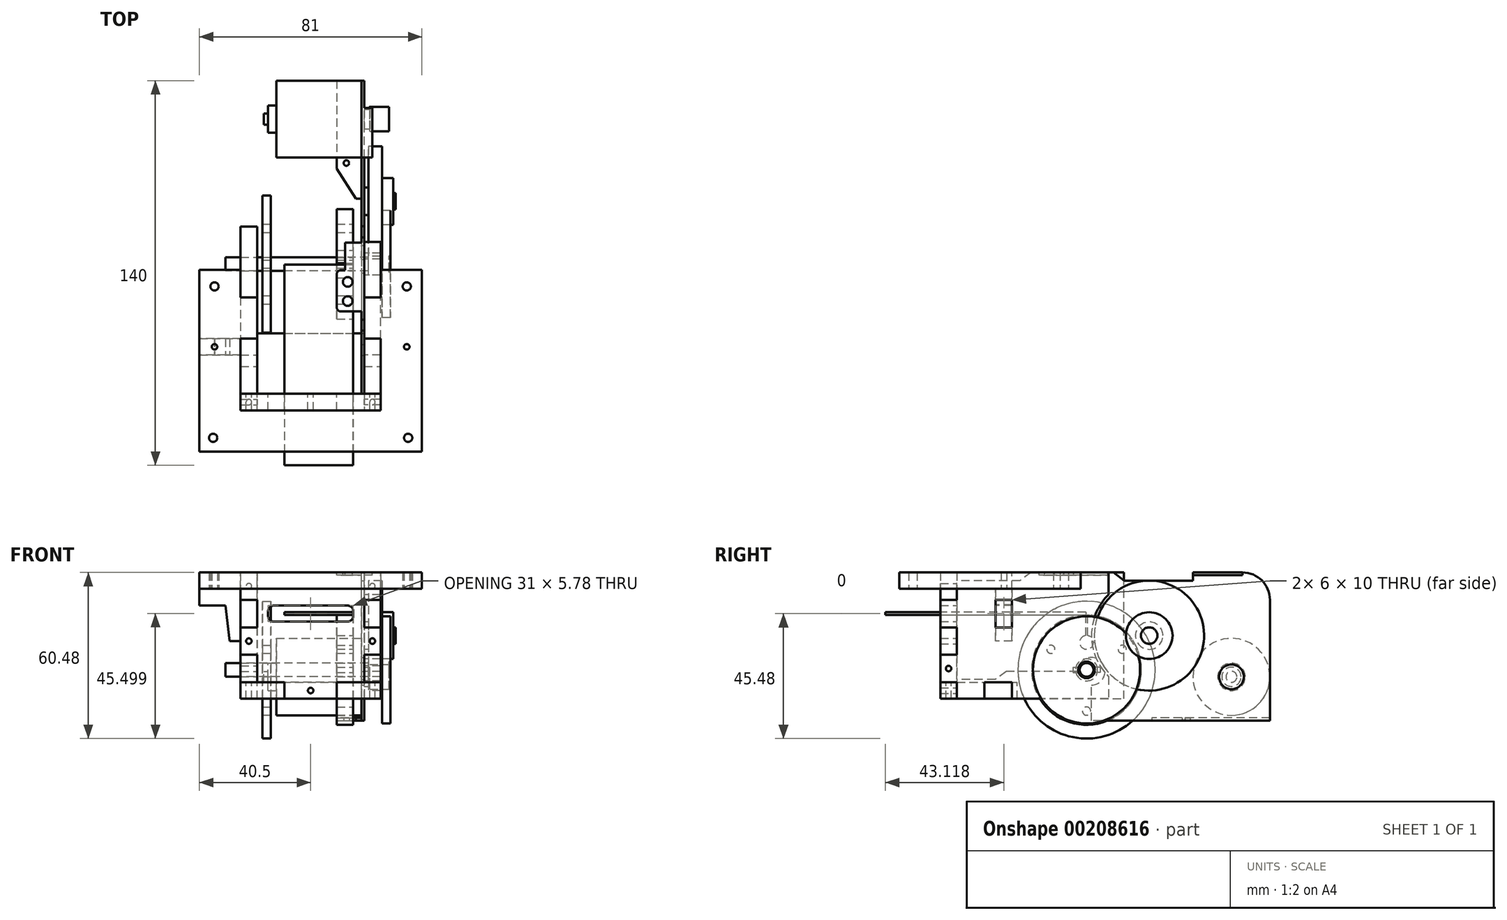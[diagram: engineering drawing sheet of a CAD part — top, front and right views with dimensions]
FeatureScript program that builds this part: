
annotation { "Feature Type Name" : "Feature", "Feature Type Description" : "" }
export const myFeature = defineFeature(function(context is Context, id is Id, definition is map)
    precondition{}
    {
        {
            var Q0;
            Q0=qCreatedBy(makeId("Top.planeOp"),FACE);
            var sketch = newSketch(context, id + "F0", { "sketchPlane" : qUnion([Q0])});
            skLineSegment(sketch, "E0.bottom", {"start": v(-32, 14) * mm, "end": v(0, 14) * mm});
            skLineSegment(sketch, "E0.left", {"start": v(-32, 14) * mm, "end": v(-32, 5) * mm});
            skLineSegment(sketch, "E0.right", {"start": v(0, 14) * mm, "end": v(0, 3.5) * mm});
            skLineSegment(sketch, "E1.top", {"start": v(0, 3.5) * mm, "end": v(2, 3.5) * mm});
            skLineSegment(sketch, "E2.top", {"start": v(2, 4.5) * mm, "end": v(9, 4.5) * mm});
            skLineSegment(sketch, "E2.left", {"start": v(2, 3.5) * mm, "end": v(2, 4.5) * mm});
            skLineSegment(sketch, "E2.right", {"start": v(9, 0) * mm, "end": v(9, 4.5) * mm});
            skLineSegment(sketch, "E3", {"start": v(-36.5, 0) * mm, "end": v(-36.5, 2) * mm});
            skLineSegment(sketch, "E4", {"start": v(-36.5, 2) * mm, "end": v(-35, 2) * mm});
            skLineSegment(sketch, "E5", {"start": v(-35, 2) * mm, "end": v(-35, 5) * mm});
            skLineSegment(sketch, "E6", {"start": v(-35, 5) * mm, "end": v(-32, 5) * mm});
            skLineSegment(sketch, "E7", {"start": v(9, 0) * mm, "end": v(-36.5, 0) * mm});
            skSolve(sketch);
        }
        {
            var Q0;
            Q0 = qSketchRegion(id + "F0", true);
            var Q1;
            Q1=sQuery(id+"F0.wireOp",EDGE,"E7");
            revolve(context, id + "F1", {"entities" : qUnion([Q0]), "axis" : qUnion([Q1]), "revolveType" : RevolveType.FULL});
        }
        {
            var Q0;
            Q0=makeQuery(id+"F1.opRevolve","SWEPT_FACE",FACE,{"disambiguationData":[OSD([sQuery(id+"F0.wireOp",EDGE,"E0.right")])]});
            var sketch = newSketch(context, id + "F2", { "sketchPlane" : qUnion([Q0])});
            skLineSegment(sketch, "E8.bottom", {"start": v(4, 38) * mm, "end": v(-14, 38) * mm});
            skLineSegment(sketch, "E8.top", {"start": v(14, -16) * mm, "end": v(-51, -16) * mm});
            skLineSegment(sketch, "E8.left", {"start": v(14, 28) * mm, "end": v(14, -16) * mm});
            skPoint(sketch, "E9.visualSharp", {"position": v(14, 38) * mm});
            skArc(sketch, "E9.filletArc", {"start": v(14, 28) * mm, "mid": v(11.07, 35.07) * mm, "end": v(4, 38) * mm});
            skLineSegment(sketch, "E10", {"start": v(-43, 38) * mm, "end": v(-39, 35) * mm});
            skLineSegment(sketch, "E11", {"start": v(-39, 35) * mm, "end": v(-14, 35) * mm});
            skLineSegment(sketch, "E12", {"start": v(-14, 35) * mm, "end": v(-14, 38) * mm});
            skLineSegment(sketch, "E13.trimOffspring", {"start": v(-43, 38) * mm, "end": v(-73, 38) * mm});
            skLineSegment(sketch, "E14", {"start": v(-51, -16) * mm, "end": v(-51, -3) * mm});
            skLineSegment(sketch, "E15", {"start": v(-56, 2) * mm, "end": v(-82, 2) * mm});
            skArc(sketch, "E16", {"start": v(-51, -3) * mm, "mid": v(-47.46, 5.54) * mm, "end": v(-56, 2) * mm});
            skLineSegment(sketch, "E17", {"start": v(-73, 38) * mm, "end": v(-77, 35) * mm});
            skLineSegment(sketch, "E18", {"start": v(-77, 35) * mm, "end": v(-100, 35) * mm});
            skLineSegment(sketch, "E19", {"start": v(-82, 2) * mm, "end": v(-86, -1) * mm});
            skLineSegment(sketch, "E20", {"start": v(-86, -1) * mm, "end": v(-100, -1) * mm});
            skLineSegment(sketch, "E21", {"start": v(-100, -1) * mm, "end": v(-100, 35) * mm});
            skPoint(sketch, "E22", {"position": v(-29.95, 15) * mm});
            skPoint(sketch, "E23", {"position": v(-52.76, 2.52) * mm});
            skSolve(sketch);
        }
        {
            var Q0;
            Q0 = qSketchRegion(id + "F2", true);
            extrude(context, id + "F3", {"entities" : qUnion([Q0]), "operationType" : NewBodyOperationType.ADD, "oppositeDirection" : true, "depth" : 1 * mm});
        }
        {
            var Q0;
            Q0=makeQuery(id+"F3.opExtrude","SWEPT_FACE",FACE,{"disambiguationData":[OSD([sQuery(id+"F2.wireOp",EDGE,"E8.top")])]});
            var sketch = newSketch(context, id + "F4", { "sketchPlane" : qUnion([Q0])});
            skLineSegment(sketch, "E24", {"start": v(-1, -14) * mm, "end": v(-10, -14) * mm});
            skLineSegment(sketch, "E25", {"start": v(-10, -14) * mm, "end": v(-10, 18) * mm});
            skLineSegment(sketch, "E26", {"start": v(-10, 18) * mm, "end": v(-3, 29) * mm});
            skLineSegment(sketch, "E27", {"start": v(-3, 29) * mm, "end": v(-1, 29) * mm});
            skLineSegment(sketch, "E28", {"start": v(-1, 29) * mm, "end": v(-1, -14) * mm});
            skCircle(sketch, "E29", {"center": v(-6.5, 16) * mm, "radius": 1 * mm});
            skSolve(sketch);
        }
        {
            var Q0;
            Q0 = qSketchRegion(id + "F4", true);
            extrude(context, id + "F5", {"entities" : qUnion([Q0]), "operationType" : NewBodyOperationType.ADD, "oppositeDirection" : true, "depth" : 1 * mm});
        }
        {
            var Q0;
            Q0=makeQuery(id+"F3.opExtrude","SWEPT_FACE",FACE,{"disambiguationData":[OSD([sQuery(id+"F2.wireOp",EDGE,"E13.trimOffspring")])]});
            var sketch = newSketch(context, id + "F6", { "sketchPlane" : qUnion([Q0])});
            skLineSegment(sketch, "E30", {"start": v(-1, -70) * mm, "end": v(-8.5, -70) * mm});
            skLineSegment(sketch, "E31", {"start": v(-10, -68.5) * mm, "end": v(-10, -56.5) * mm});
            skLineSegment(sketch, "E32", {"start": v(-8.5, -55) * mm, "end": v(-7, -55) * mm});
            skLineSegment(sketch, "E33", {"start": v(-7, -55) * mm, "end": v(-7, -45) * mm});
            skLineSegment(sketch, "E34", {"start": v(-7, -45) * mm, "end": v(-1, -45) * mm});
            skLineSegment(sketch, "E35", {"start": v(-1, -45) * mm, "end": v(-1, -70) * mm});
            skPoint(sketch, "E36.visualSharp", {"position": v(-10, -55) * mm});
            skArc(sketch, "E36.filletArc", {"start": v(-8.5, -55) * mm, "mid": v(-9.56, -55.44) * mm, "end": v(-10, -56.5) * mm});
            skCircle(sketch, "E37", {"center": v(-6, -66.25) * mm, "radius": 1.75 * mm});
            skLineSegment(sketch, "E38", {"start": v(-6, -66.25) * mm, "end": v(-6, -59.25) * mm, "construction": true});
            skCircle(sketch, "E39", {"center": v(-6, -59.25) * mm, "radius": 1.75 * mm});
            skLineSegment(sketch, "E40", {"start": v(0, 4) * mm, "end": v(3, 4) * mm});
            skLineSegment(sketch, "E41", {"start": v(3, 4) * mm, "end": v(3, -14) * mm});
            skLineSegment(sketch, "E42", {"start": v(3, -14) * mm, "end": v(0, -14) * mm});
            skLineSegment(sketch, "E43", {"start": v(0, -14) * mm, "end": v(0, 4) * mm});
            skPoint(sketch, "E44.visualSharp", {"position": v(-10, -70) * mm});
            skArc(sketch, "E44.filletArc", {"start": v(-10, -68.5) * mm, "mid": v(-9.56, -69.56) * mm, "end": v(-8.5, -70) * mm});
            skSolve(sketch);
        }
        {
            var Q0;
            Q0 = qSketchRegion(id + "F6", true);
            extrude(context, id + "F7", {"entities" : qUnion([Q0]), "operationType" : NewBodyOperationType.ADD, "oppositeDirection" : true, "depth" : 1 * mm});
        }
        {
            var Q0;
            Q0=sQuery(id+"F2.wireOp",VERTEX,"E22");
            var Q1;
            Q1=sQuery(id+"F2.wireOp",EDGE,"E12");
            cPlane(context, id + "F8", {"entities" : qUnion([Q0, Q1]), "cplaneType" : CPlaneType.LINE_POINT, "offset" : 25 * mm, "width" : 150 * mm, "height" : 150 * mm});
        }
        {
            var Q0;
            Q0=qCreatedBy(id+"F8.planeOp",FACE);
            var sketch = newSketch(context, id + "F9", { "sketchPlane" : qUnion([Q0])});
            skLineSegment(sketch, "E45", {"start": v(0, -29.95) * mm, "end": v(11.5, -29.95) * mm});
            skLineSegment(sketch, "E46", {"start": v(11.5, -29.95) * mm, "end": v(11.5, -26.95) * mm});
            skLineSegment(sketch, "E47", {"start": v(11.5, -26.95) * mm, "end": v(10.5, -26.95) * mm});
            skLineSegment(sketch, "E48", {"start": v(10.5, -26.95) * mm, "end": v(10.5, -21.45) * mm});
            skLineSegment(sketch, "E49", {"start": v(10.5, -21.45) * mm, "end": v(6.5, -21.45) * mm});
            skLineSegment(sketch, "E50", {"start": v(6.5, -21.45) * mm, "end": v(6.5, -9.95) * mm});
            skLineSegment(sketch, "E51", {"start": v(6.5, -9.95) * mm, "end": v(1.5, -9.95) * mm});
            skLineSegment(sketch, "E52", {"start": v(1.5, -9.95) * mm, "end": v(1.5, -24.95) * mm});
            skLineSegment(sketch, "E53", {"start": v(1.5, -24.95) * mm, "end": v(0, -24.95) * mm});
            skLineSegment(sketch, "E54", {"start": v(0, -24.95) * mm, "end": v(0, -29.95) * mm});
            skSolve(sketch);
        }
        {
            var Q0;
            Q0 = qSketchRegion(id + "F9", true);
            var Q1;
            Q1=sQuery(id+"F9.wireOp",EDGE,"E45");
            revolve(context, id + "F10", {"operationType" : NewBodyOperationType.ADD, "entities" : qUnion([Q0]), "axis" : qUnion([Q1]), "revolveType" : RevolveType.FULL});
        }
        {
            var Q0;
            Q0=sQuery(id+"F2.wireOp",VERTEX,"E23");
            var Q1;
            Q1=sQuery(id+"F2.wireOp",EDGE,"E21");
            cPlane(context, id + "F11", {"entities" : qUnion([Q0, Q1]), "cplaneType" : CPlaneType.LINE_POINT, "offset" : 25 * mm, "width" : 150 * mm, "height" : 150 * mm});
        }
        {
            var Q0;
            Q0=qCreatedBy(id+"F11.planeOp",FACE);
            var sketch = newSketch(context, id + "F12", { "sketchPlane" : qUnion([Q0])});
            skLineSegment(sketch, "E55", {"start": v(-50.5, -52.76) * mm, "end": v(9.5, -52.76) * mm});
            skLineSegment(sketch, "E56", {"start": v(9.5, -52.76) * mm, "end": v(9.5, -50.26) * mm});
            skLineSegment(sketch, "E57", {"start": v(9.5, -33.26) * mm, "end": v(6.5, -33.26) * mm});
            skLineSegment(sketch, "E58", {"start": v(6.5, -33.26) * mm, "end": v(6.5, -48.76) * mm});
            skLineSegment(sketch, "E59", {"start": v(6.5, -48.76) * mm, "end": v(1.5, -48.76) * mm});
            skLineSegment(sketch, "E60", {"start": v(1.5, -48.76) * mm, "end": v(1.5, -50.26) * mm});
            skLineSegment(sketch, "E61", {"start": v(1.5, -50.26) * mm, "end": v(-50.5, -50.26) * mm});
            skLineSegment(sketch, "E62", {"start": v(-50.5, -50.26) * mm, "end": v(-50.5, -52.76) * mm});
            skLineSegment(sketch, "E63", {"start": v(9.5, -50.26) * mm, "end": v(9, -50.26) * mm});
            skLineSegment(sketch, "E64", {"start": v(9, -50.26) * mm, "end": v(9, -49.76) * mm});
            skLineSegment(sketch, "E65", {"start": v(9.5, -50.26) * mm, "end": v(9.5, -49.76) * mm, "construction": true});
            skLineSegment(sketch, "E66", {"start": v(9.5, -49.76) * mm, "end": v(9.5, -33.26) * mm});
            skLineSegment(sketch, "E67", {"start": v(9.5, -49.76) * mm, "end": v(9, -49.76) * mm});
            skSolve(sketch);
        }
        {
            var Q0;
            Q0 = qSketchRegion(id + "F12", true);
            var Q1;
            Q1=sQuery(id+"F12.wireOp",EDGE,"E55");
            revolve(context, id + "F13", {"entities" : qUnion([Q0]), "axis" : qUnion([Q1]), "revolveType" : RevolveType.FULL});
        }
        {
            var Q0;
            Q0=makeQuery(id+"F3.boolean.opBoolean","MERGE",FACE,{"derivedFrom":[makeQuery(id+"F1.opRevolve","SWEPT_FACE",FACE,{"disambiguationData":[OSD([sQuery(id+"F0.wireOp",EDGE,"E0.right")])]}),makeQuery(id+"F3.opExtrude","CAP_FACE",FACE,{"disambiguationData":[OSD([sQuery(id+"F2.wireOp",EDGE,"E8.bottom"),sQuery(id+"F2.wireOp",EDGE,"E8.top"),sQuery(id+"F2.wireOp",EDGE,"E8.left"),sQuery(id+"F2.wireOp",EDGE,"E9.filletArc"),sQuery(id+"F2.wireOp",EDGE,"E10"),sQuery(id+"F2.wireOp",EDGE,"E11"),sQuery(id+"F2.wireOp",EDGE,"E12"),sQuery(id+"F2.wireOp",EDGE,"E13.trimOffspring"),sQuery(id+"F2.wireOp",EDGE,"E14"),sQuery(id+"F2.wireOp",EDGE,"E15"),sQuery(id+"F2.wireOp",EDGE,"E16"),sQuery(id+"F2.wireOp",EDGE,"E17"),sQuery(id+"F2.wireOp",EDGE,"E18"),sQuery(id+"F2.wireOp",EDGE,"E19"),sQuery(id+"F2.wireOp",EDGE,"E20"),sQuery(id+"F2.wireOp",EDGE,"E21")])],"isStart":true})]});
            var sketch = newSketch(context, id + "F14", { "sketchPlane" : qUnion([Q0])});
            skLineSegment(sketch, "E68.top", {"start": v(-106, -8) * mm, "end": v(-100, -8) * mm, "construction": true});
            skCircle(sketch, "E69", {"center": v(-52.76, 2.52) * mm, "radius": 4 * mm});
            skArc(sketch, "E70", {"start": v(-44.76, 29.89) * mm, "mid": v(-50.95, 15) * mm, "end": v(-44.76, 0.11) * mm});
            skLineSegment(sketch, "E71", {"start": v(-44.76, 0.11) * mm, "end": v(-44.76, -8) * mm});
            skLineSegment(sketch, "E72", {"start": v(-106, 38) * mm, "end": v(-100, 38) * mm});
            skLineSegment(sketch, "E73", {"start": v(-44.76, 38) * mm, "end": v(-44.76, 29.89) * mm});
            skLineSegment(sketch, "E74", {"start": v(-100, 38) * mm, "end": v(-79.88, 38) * mm});
            skLineSegment(sketch, "E75", {"start": v(-100, 38) * mm, "end": v(-100, 28) * mm});
            skLineSegment(sketch, "E76", {"start": v(-100, 28) * mm, "end": v(-106, 28) * mm});
            skLineSegment(sketch, "E77", {"start": v(-106, 28) * mm, "end": v(-106, 18) * mm});
            skLineSegment(sketch, "E78", {"start": v(-106, 18) * mm, "end": v(-100, 18) * mm});
            skLineSegment(sketch, "E79", {"start": v(-100, 18) * mm, "end": v(-100, 8) * mm});
            skLineSegment(sketch, "E80", {"start": v(-100, 8) * mm, "end": v(-106, 8) * mm});
            skLineSegment(sketch, "E81", {"start": v(-106, 8) * mm, "end": v(-106, -2) * mm});
            skLineSegment(sketch, "E82", {"start": v(-106, -2) * mm, "end": v(-100, -2) * mm});
            skLineSegment(sketch, "E83", {"start": v(-100, -2) * mm, "end": v(-100, -8) * mm});
            skLineSegment(sketch, "E84", {"start": v(-90, -8) * mm, "end": v(-90, -2) * mm});
            skLineSegment(sketch, "E85", {"start": v(-90, -2) * mm, "end": v(-80, -2) * mm});
            skLineSegment(sketch, "E86", {"start": v(-80, -2) * mm, "end": v(-80, -8) * mm});
            skLineSegment(sketch, "E87", {"start": v(-44.76, -8) * mm, "end": v(-80, -8) * mm});
            skLineSegment(sketch, "E88", {"start": v(-90, -8) * mm, "end": v(-100, -8) * mm});
            skLineSegment(sketch, "E89", {"start": v(-106, 8) * mm, "end": v(-100, -2) * mm, "construction": true});
            skCircle(sketch, "E90", {"center": v(-103, 3) * mm, "radius": 1 * mm});
            skLineSegment(sketch, "E91", {"start": v(-79.88, 38) * mm, "end": v(-79.88, 32) * mm});
            skLineSegment(sketch, "E92", {"start": v(-79.88, 32) * mm, "end": v(-64.88, 32) * mm});
            skLineSegment(sketch, "E93", {"start": v(-64.88, 32) * mm, "end": v(-64.88, 38) * mm});
            skLineSegment(sketch, "E94.trimOffspring", {"start": v(-64.88, 38) * mm, "end": v(-44.76, 38) * mm});
            skLineSegment(sketch, "E95.bottom", {"start": v(-85.88, 28) * mm, "end": v(-79.88, 28) * mm});
            skLineSegment(sketch, "E95.top", {"start": v(-85.88, 18) * mm, "end": v(-79.88, 18) * mm});
            skLineSegment(sketch, "E95.left", {"start": v(-85.88, 28) * mm, "end": v(-85.88, 18) * mm});
            skLineSegment(sketch, "E95.right", {"start": v(-79.88, 28) * mm, "end": v(-79.88, 18) * mm});
            skSolve(sketch);
        }
        {
            var Q0;
            Q0 = qSketchRegion(id + "F14", true);
            extrude(context, id + "F15", {"entities" : qUnion([Q0]), "depth" : 6 * mm});
        }
        {
            var Q0;
            Q0=makeQuery(id+"F3.opExtrude","CAP_FACE",FACE,{"disambiguationData":[OSD([sQuery(id+"F2.wireOp",EDGE,"E8.bottom"),sQuery(id+"F2.wireOp",EDGE,"E8.top"),sQuery(id+"F2.wireOp",EDGE,"E8.left"),sQuery(id+"F2.wireOp",EDGE,"E9.filletArc"),sQuery(id+"F2.wireOp",EDGE,"E10"),sQuery(id+"F2.wireOp",EDGE,"E11"),sQuery(id+"F2.wireOp",EDGE,"E12"),sQuery(id+"F2.wireOp",EDGE,"E13.trimOffspring"),sQuery(id+"F2.wireOp",EDGE,"E14"),sQuery(id+"F2.wireOp",EDGE,"E15"),sQuery(id+"F2.wireOp",EDGE,"E16"),sQuery(id+"F2.wireOp",EDGE,"E17"),sQuery(id+"F2.wireOp",EDGE,"E18"),sQuery(id+"F2.wireOp",EDGE,"E19"),sQuery(id+"F2.wireOp",EDGE,"E20"),sQuery(id+"F2.wireOp",EDGE,"E21")])],"isStart":false});
            cPlane(context, id + "F16", {"entities" : qUnion([Q0]), "cplaneType" : CPlaneType.OFFSET, "offset" : 3 * mm, "width" : 150 * mm, "height" : 150 * mm});
        }
        {
            var Q0;
            Q0=qCreatedBy(id+"F16.planeOp",FACE);
            var sketch = newSketch(context, id + "F17", { "sketchPlane" : qUnion([Q0])});
            skArc(sketch, "E96", {"start": v(52.51, 22.52) * mm, "mid": v(52.76, -17.48) * mm, "end": v(53.01, 22.52) * mm});
            skArc(sketch, "E97", {"start": v(55.05, 3.52) * mm, "mid": v(52.76, 5.02) * mm, "end": v(50.47, 3.52) * mm});
            skLineSegment(sketch, "E98", {"start": v(52.51, 22.52) * mm, "end": v(52.51, 15) * mm});
            skLineSegment(sketch, "E99", {"start": v(52.51, 12.52) * mm, "end": v(53.01, 12.52) * mm, "construction": true});
            skLineSegment(sketch, "E100", {"start": v(53.01, 12.52) * mm, "end": v(53.01, 15) * mm, "construction": true});
            skLineSegment(sketch, "E101", {"start": v(52.76, 2.52) * mm, "end": v(52.76, 12.52) * mm, "construction": true});
            skArc(sketch, "E102", {"start": v(52.51, 15) * mm, "mid": v(52.76, 10.02) * mm, "end": v(53.01, 15) * mm});
            skLineSegment(sketch, "E103", {"start": v(52.51, 15) * mm, "end": v(52.51, 12.52) * mm, "construction": true});
            skLineSegment(sketch, "E104", {"start": v(53.01, 15) * mm, "end": v(53.01, 22.52) * mm});
            skCircle(sketch, "E105", {"center": v(39.77, 10.02) * mm, "radius": 1.5 * mm});
            skCircle(sketch, "E106", {"center": v(65.75, 10.02) * mm, "radius": 1.5 * mm});
            skCircle(sketch, "E107", {"center": v(52.76, -12.48) * mm, "radius": 1.5 * mm});
            skLineSegment(sketch, "E108", {"start": v(39.77, 10.02) * mm, "end": v(52.76, 2.52) * mm, "construction": true});
            skLineSegment(sketch, "E109", {"start": v(65.75, 10.02) * mm, "end": v(52.76, 2.52) * mm, "construction": true});
            skLineSegment(sketch, "E110", {"start": v(52.76, -12.48) * mm, "end": v(52.76, 2.52) * mm, "construction": true});
            skLineSegment(sketch, "E111", {"start": v(47.76, 2.52) * mm, "end": v(57.76, 2.52) * mm, "construction": true});
            skLineSegment(sketch, "E112", {"start": v(57.76, 3.52) * mm, "end": v(57.76, 1.52) * mm});
            skLineSegment(sketch, "E113", {"start": v(57.76, 3.52) * mm, "end": v(55.05, 3.52) * mm});
            skLineSegment(sketch, "E114", {"start": v(57.76, 1.52) * mm, "end": v(55.05, 1.52) * mm});
            skLineSegment(sketch, "E115", {"start": v(47.76, 3.52) * mm, "end": v(47.76, 1.52) * mm});
            skLineSegment(sketch, "E116", {"start": v(47.76, 3.52) * mm, "end": v(50.47, 3.52) * mm});
            skLineSegment(sketch, "E117", {"start": v(47.76, 1.52) * mm, "end": v(50.47, 1.52) * mm});
            skArc(sketch, "E118.trimOffspring", {"start": v(50.47, 1.52) * mm, "mid": v(52.76, 0.02) * mm, "end": v(55.05, 1.52) * mm});
            skSolve(sketch);
        }
        {
            var Q0;
            Q0 = qSketchRegion(id + "F17", true);
            extrude(context, id + "F18", {"entities" : qUnion([Q0]), "depth" : 6 * mm});
        }
        {
            var Q0;
            Q0=makeQuery(id+"F18.opExtrude","CAP_FACE",FACE,{"disambiguationData":[OSD([sQuery(id+"F17.wireOp",EDGE,"E96"),sQuery(id+"F17.wireOp",EDGE,"E97"),sQuery(id+"F17.wireOp",EDGE,"E98"),sQuery(id+"F17.wireOp",EDGE,"E102"),sQuery(id+"F17.wireOp",EDGE,"E104"),sQuery(id+"F17.wireOp",EDGE,"E105"),sQuery(id+"F17.wireOp",EDGE,"E106"),sQuery(id+"F17.wireOp",EDGE,"E107")])],"isStart":false});
            cPlane(context, id + "F19", {"entities" : qUnion([Q0]), "cplaneType" : CPlaneType.OFFSET, "offset" : (4 * 6) * mm, "width" : 150 * mm, "height" : 150 * mm});
        }
        {
            var Q0;
            Q0=qCreatedBy(id+"F19.planeOp",FACE);
            var sketch = newSketch(context, id + "F20", { "sketchPlane" : qUnion([Q0])});
            skCircle(sketch, "E119", {"center": v(52.76, 2.52) * mm, "radius": 25 * mm});
            skCircle(sketch, "E120", {"center": v(65.75, 10.02) * mm, "radius": 1.5 * mm});
            skCircle(sketch, "E121", {"center": v(39.77, 10.02) * mm, "radius": 1.5 * mm});
            skCircle(sketch, "E122", {"center": v(52.76, -12.48) * mm, "radius": 1.5 * mm});
            skCircle(sketch, "E123", {"center": v(52.76, 2.52) * mm, "radius": 2.5 * mm});
            skSolve(sketch);
        }
        {
            var Q0;
            Q0 = qSketchRegion(id + "F20", true);
            extrude(context, id + "F21", {"entities" : qUnion([Q0]), "depth" : 3 * mm});
        }
        {
            var Q0;
            Q0=makeQuery(id+"F18.opExtrude","CAP_FACE",FACE,{"disambiguationData":[OSD([sQuery(id+"F17.wireOp",EDGE,"E96"),sQuery(id+"F17.wireOp",EDGE,"E97"),sQuery(id+"F17.wireOp",EDGE,"E98"),sQuery(id+"F17.wireOp",EDGE,"E102"),sQuery(id+"F17.wireOp",EDGE,"E104"),sQuery(id+"F17.wireOp",EDGE,"E105"),sQuery(id+"F17.wireOp",EDGE,"E106"),sQuery(id+"F17.wireOp",EDGE,"E107")])],"isStart":true});
            var sketch = newSketch(context, id + "F22", { "sketchPlane" : qUnion([Q0])});
            skLineSegment(sketch, "E124", {"start": v(-126, 22.52) * mm, "end": v(-53.01, 22.52) * mm});
            skLineSegment(sketch, "E125", {"start": v(-126, 22.52) * mm, "end": v(-126, 23.52) * mm});
            skLineSegment(sketch, "E126", {"start": v(-53.01, 23.52) * mm, "end": v(-126, 23.52) * mm});
            skLineSegment(sketch, "E127", {"start": v(-53.01, 23.52) * mm, "end": v(-53.01, 22.52) * mm});
            skSolve(sketch);
        }
        {
            var Q0;
            Q0 = qSketchRegion(id + "F22", true);
            extrude(context, id + "F23", {"entities" : qUnion([Q0]), "oppositeDirection" : true, "depth" : 25 * mm});
        }
        {
            var Q0;
            Q0=makeQuery(id+"F15.opExtrude","SWEPT_FACE",FACE,{"disambiguationData":[OSD([sQuery(id+"F14.wireOp",EDGE,"E75")])]});
            var sketch = newSketch(context, id + "F24", { "sketchPlane" : qUnion([Q0])});
            skLineSegment(sketch, "E128", {"start": v(6, 38) * mm, "end": v(-19.5, 38) * mm});
            skLineSegment(sketch, "E129", {"start": v(6, 38) * mm, "end": v(6, 28) * mm});
            skLineSegment(sketch, "E130", {"start": v(6, 28) * mm, "end": v(0, 28) * mm});
            skLineSegment(sketch, "E131", {"start": v(0, 28) * mm, "end": v(0, 18) * mm});
            skLineSegment(sketch, "E132", {"start": v(0, 18) * mm, "end": v(6, 18) * mm});
            skLineSegment(sketch, "E133", {"start": v(6, 18) * mm, "end": v(6, 8) * mm});
            skLineSegment(sketch, "E134", {"start": v(6, 8) * mm, "end": v(0, 8) * mm});
            skLineSegment(sketch, "E135", {"start": v(0, 8) * mm, "end": v(0, -2) * mm});
            skLineSegment(sketch, "E136", {"start": v(-19.5, -8) * mm, "end": v(-19.5, -2) * mm, "construction": true});
            skLineSegment(sketch, "E137", {"start": v(0, -2) * mm, "end": v(-10, -2) * mm});
            skLineSegment(sketch, "E138", {"start": v(-10, -2) * mm, "end": v(-10, -8) * mm});
            skLineSegment(sketch, "E139", {"start": v(-10, -8) * mm, "end": v(-19.5, -8) * mm});
            skLineSegment(sketch, "E140.bottom", {"start": v(-6, 20.13) * mm, "end": v(-33, 20.13) * mm});
            skLineSegment(sketch, "E140.top", {"start": v(-6, 25.9) * mm, "end": v(-33, 25.9) * mm});
            skLineSegment(sketch, "E140.left", {"start": v(-4, 22.13) * mm, "end": v(-4, 23.9) * mm});
            skLineSegment(sketch, "E140.right", {"start": v(-35, 22.13) * mm, "end": v(-35, 23.9) * mm});
            skPoint(sketch, "E140.middle", {"position": v(-19.5, 23.02) * mm});
            skPoint(sketch, "E141.visualSharp", {"position": v(-4, 25.9) * mm});
            skArc(sketch, "E141.filletArc", {"start": v(-4, 23.9) * mm, "mid": v(-4.59, 25.32) * mm, "end": v(-6, 25.9) * mm});
            skPoint(sketch, "E142.visualSharp", {"position": v(-4, 20.13) * mm});
            skArc(sketch, "E142.filletArc", {"start": v(-6, 20.13) * mm, "mid": v(-4.59, 20.72) * mm, "end": v(-4, 22.13) * mm});
            skPoint(sketch, "E143.visualSharp", {"position": v(-35, 20.13) * mm});
            skArc(sketch, "E143.filletArc", {"start": v(-35, 22.13) * mm, "mid": v(-34.41, 20.72) * mm, "end": v(-33, 20.13) * mm});
            skPoint(sketch, "E144.visualSharp", {"position": v(-35, 25.9) * mm});
            skArc(sketch, "E144.filletArc", {"start": v(-33, 25.9) * mm, "mid": v(-34.41, 25.32) * mm, "end": v(-35, 23.9) * mm});
            skLineSegment(sketch, "E145", {"start": v(-29, 23.02) * mm, "end": v(-19.5, 23.02) * mm, "construction": true});
            skLineSegment(sketch, "E146.MirrorCS", {"start": v(-45, 38) * mm, "end": v(-19.5, 38) * mm});
            skLineSegment(sketch, "E147.MirrorCS", {"start": v(-45, 38) * mm, "end": v(-45, 28) * mm});
            skLineSegment(sketch, "E148.MirrorCS", {"start": v(-45, 28) * mm, "end": v(-39, 28) * mm});
            skLineSegment(sketch, "E149.MirrorCS", {"start": v(-39, 28) * mm, "end": v(-39, 18) * mm});
            skLineSegment(sketch, "E150.MirrorCS", {"start": v(-39, 18) * mm, "end": v(-45, 18) * mm});
            skLineSegment(sketch, "E151.MirrorCS", {"start": v(-45, 18) * mm, "end": v(-45, 8) * mm});
            skLineSegment(sketch, "E152.MirrorCS", {"start": v(-45, 8) * mm, "end": v(-39, 8) * mm});
            skLineSegment(sketch, "E153.MirrorCS", {"start": v(-39, 8) * mm, "end": v(-39, -2) * mm});
            skLineSegment(sketch, "E154.MirrorCS", {"start": v(-39, -2) * mm, "end": v(-29, -2) * mm});
            skLineSegment(sketch, "E155.MirrorCS", {"start": v(-29, -8) * mm, "end": v(-19.5, -8) * mm});
            skLineSegment(sketch, "E156.MirrorCS", {"start": v(-29, -2) * mm, "end": v(-29, -8) * mm});
            skLineSegment(sketch, "E157", {"start": v(-19.5, -2) * mm, "end": v(-19.5, 38) * mm, "construction": true});
            skCircle(sketch, "E158", {"center": v(-19.5, -5) * mm, "radius": 1 * mm});
            skLineSegment(sketch, "E159", {"start": v(3, 13) * mm, "end": v(-42, 13) * mm, "construction": true});
            skPoint(sketch, "E160", {"position": v(-19.5, 13) * mm});
            skCircle(sketch, "E161", {"center": v(3, 13) * mm, "radius": 1 * mm});
            skCircle(sketch, "E162", {"center": v(-42, 13) * mm, "radius": 1 * mm});
            skLineSegment(sketch, "E163", {"start": v(-42, 33) * mm, "end": v(3, 33) * mm, "construction": true});
            skPoint(sketch, "E164", {"position": v(-19.5, 33) * mm});
            skCircle(sketch, "E165", {"center": v(-42, 33) * mm, "radius": 1 * mm});
            skCircle(sketch, "E166", {"center": v(3, 33) * mm, "radius": 1 * mm});
            skSolve(sketch);
        }
        {
            var Q0;
            Q0 = qSketchRegion(id + "F24", true);
            extrude(context, id + "F25", {"entities" : qUnion([Q0]), "depth" : 6 * mm});
        }
        {
            var Q0;
            Q0=makeQuery(id+"F25.opExtrude","SWEPT_FACE",FACE,{"disambiguationData":[OSD([sQuery(id+"F24.wireOp",EDGE,"E137")])]});
            var sketch = newSketch(context, id + "F26", { "sketchPlane" : qUnion([Q0])});
            skLineSegment(sketch, "E167", {"start": v(-10, 106) * mm, "end": v(-10, 100) * mm});
            skLineSegment(sketch, "E168", {"start": v(-10, 100) * mm, "end": v(-19.5, 100) * mm});
            skLineSegment(sketch, "E169", {"start": v(-10, 106) * mm, "end": v(6, 106) * mm});
            skLineSegment(sketch, "E170", {"start": v(6, 106) * mm, "end": v(6, 100) * mm});
            skLineSegment(sketch, "E171", {"start": v(6, 100) * mm, "end": v(0, 100) * mm});
            skLineSegment(sketch, "E172", {"start": v(0, 100) * mm, "end": v(0, 90) * mm});
            skLineSegment(sketch, "E173", {"start": v(0, 90) * mm, "end": v(6, 90) * mm});
            skLineSegment(sketch, "E174", {"start": v(6, 90) * mm, "end": v(6, 80) * mm});
            skLineSegment(sketch, "E175", {"start": v(6, 80) * mm, "end": v(0, 80) * mm});
            skLineSegment(sketch, "E176", {"start": v(0, 80) * mm, "end": v(0, 78) * mm});
            skLineSegment(sketch, "E177", {"start": v(0, 78) * mm, "end": v(-19.5, 78) * mm});
            skLineSegment(sketch, "E178", {"start": v(-19.5, 78) * mm, "end": v(-19.5, 100) * mm, "construction": true});
            skLineSegment(sketch, "E179.MirrorCS", {"start": v(-29, 100) * mm, "end": v(-19.5, 100) * mm});
            skLineSegment(sketch, "E180.MirrorCS", {"start": v(-29, 106) * mm, "end": v(-29, 100) * mm});
            skLineSegment(sketch, "E181.MirrorCS", {"start": v(-29, 106) * mm, "end": v(-45, 106) * mm});
            skLineSegment(sketch, "E182.MirrorCS", {"start": v(-45, 106) * mm, "end": v(-45, 100) * mm});
            skLineSegment(sketch, "E183.MirrorCS", {"start": v(-45, 100) * mm, "end": v(-39, 100) * mm});
            skLineSegment(sketch, "E184.MirrorCS", {"start": v(-39, 100) * mm, "end": v(-39, 90) * mm});
            skLineSegment(sketch, "E185.MirrorCS", {"start": v(-39, 90) * mm, "end": v(-45, 90) * mm});
            skLineSegment(sketch, "E186.MirrorCS", {"start": v(-45, 90) * mm, "end": v(-45, 80) * mm});
            skLineSegment(sketch, "E187.MirrorCS", {"start": v(-45, 80) * mm, "end": v(-39, 80) * mm});
            skLineSegment(sketch, "E188.MirrorCS", {"start": v(-39, 78) * mm, "end": v(-19.5, 78) * mm});
            skLineSegment(sketch, "E189.MirrorCS", {"start": v(-39, 80) * mm, "end": v(-39, 78) * mm});
            skLineSegment(sketch, "E190", {"start": v(6, 100) * mm, "end": v(0, 106) * mm, "construction": true});
            skCircle(sketch, "E191", {"center": v(3, 103) * mm, "radius": 1 * mm});
            skLineSegment(sketch, "E192", {"start": v(-39, 100) * mm, "end": v(-45, 106) * mm, "construction": true});
            skCircle(sketch, "E193", {"center": v(-42, 103) * mm, "radius": 1 * mm});
            skSolve(sketch);
        }
        {
            var Q0;
            Q0 = qSketchRegion(id + "F26", true);
            extrude(context, id + "F27", {"entities" : qUnion([Q0]), "depth" : 6 * mm});
        }
        {
            var Q0;
            Q0=makeQuery(id+"F27.opExtrude","SWEPT_FACE",FACE,{"disambiguationData":[OSD([sQuery(id+"F26.wireOp",EDGE,"E184.MirrorCS")])]});
            var sketch = newSketch(context, id + "F28", { "sketchPlane" : qUnion([Q0])});
            skLineSegment(sketch, "E194", {"start": v(39.1, 38) * mm, "end": v(64.88, 38) * mm});
            skLineSegment(sketch, "E195", {"start": v(100, 38) * mm, "end": v(100, 28) * mm});
            skLineSegment(sketch, "E196", {"start": v(100, 28) * mm, "end": v(106, 28) * mm});
            skLineSegment(sketch, "E197", {"start": v(106, 28) * mm, "end": v(106, 18) * mm});
            skLineSegment(sketch, "E198", {"start": v(106, 18) * mm, "end": v(100, 18) * mm});
            skLineSegment(sketch, "E199", {"start": v(100, 18) * mm, "end": v(100, 8) * mm});
            skLineSegment(sketch, "E200", {"start": v(100, 8) * mm, "end": v(106, 8) * mm});
            skLineSegment(sketch, "E201", {"start": v(106, 8) * mm, "end": v(106, -2) * mm});
            skLineSegment(sketch, "E202", {"start": v(106, -2) * mm, "end": v(100, -2) * mm});
            skLineSegment(sketch, "E203", {"start": v(100, -2) * mm, "end": v(100, -8) * mm});
            skLineSegment(sketch, "E204", {"start": v(100, -8) * mm, "end": v(90, -8) * mm});
            skLineSegment(sketch, "E205", {"start": v(90, -8) * mm, "end": v(90, -2) * mm});
            skLineSegment(sketch, "E206", {"start": v(90, -2) * mm, "end": v(80, -2) * mm});
            skLineSegment(sketch, "E207", {"start": v(80, -2) * mm, "end": v(80, -8) * mm});
            skLineSegment(sketch, "E208", {"start": v(80, -8) * mm, "end": v(39.1, -8) * mm});
            skLineSegment(sketch, "E209", {"start": v(39.1, -8) * mm, "end": v(39.1, 38) * mm});
            skCircle(sketch, "E210", {"center": v(52.76, 2.52) * mm, "radius": 2.5 * mm});
            skLineSegment(sketch, "E211", {"start": v(100, 8) * mm, "end": v(106, -2) * mm, "construction": true});
            skCircle(sketch, "E212", {"center": v(103, 3) * mm, "radius": 1 * mm});
            skLineSegment(sketch, "E213", {"start": v(64.88, 38) * mm, "end": v(64.88, 32) * mm});
            skLineSegment(sketch, "E214", {"start": v(64.88, 32) * mm, "end": v(79.88, 32) * mm});
            skLineSegment(sketch, "E215", {"start": v(79.88, 32) * mm, "end": v(79.88, 38) * mm});
            skLineSegment(sketch, "E216.trimOffspring", {"start": v(79.88, 38) * mm, "end": v(100, 38) * mm});
            skLineSegment(sketch, "E217.bottom", {"start": v(85.88, 18) * mm, "end": v(79.88, 18) * mm});
            skLineSegment(sketch, "E217.top", {"start": v(85.88, 28) * mm, "end": v(79.88, 28) * mm});
            skLineSegment(sketch, "E217.left", {"start": v(85.88, 18) * mm, "end": v(85.88, 28) * mm});
            skLineSegment(sketch, "E217.right", {"start": v(79.88, 18) * mm, "end": v(79.88, 28) * mm});
            skPoint(sketch, "E217.middle", {"position": v(82.88, 23) * mm});
            skSolve(sketch);
        }
        {
            var Q0;
            Q0 = qSketchRegion(id + "F28", true);
            extrude(context, id + "F29", {"entities" : qUnion([Q0]), "depth" : 6 * mm});
        }
        {
            var Q0;
            Q0=makeQuery(id+"F29.opExtrude","SWEPT_FACE",FACE,{"disambiguationData":[OSD([sQuery(id+"F28.wireOp",EDGE,"E214")])]});
            var sketch = newSketch(context, id + "F30", { "sketchPlane" : qUnion([Q0])});
            skLineSegment(sketch, "E218.bottom", {"start": v(21, -121) * mm, "end": v(-60, -121) * mm});
            skLineSegment(sketch, "E218.top", {"start": v(21, -54.88) * mm, "end": v(6, -54.88) * mm});
            skLineSegment(sketch, "E218.left", {"start": v(21, -121) * mm, "end": v(21, -54.88) * mm});
            skLineSegment(sketch, "E218.right", {"start": v(-60, -121) * mm, "end": v(-60, -54.88) * mm});
            skPoint(sketch, "E218.middle", {"position": v(-19.5, -87.94) * mm});
            skLineSegment(sketch, "E219", {"start": v(-19.5, -100) * mm, "end": v(-19.5, -87.94) * mm, "construction": true});
            skLineSegment(sketch, "E220", {"start": v(-45, -54.88) * mm, "end": v(-45, -64.88) * mm});
            skLineSegment(sketch, "E221", {"start": v(-45, -64.88) * mm, "end": v(-39, -64.88) * mm});
            skLineSegment(sketch, "E222", {"start": v(-39, -64.88) * mm, "end": v(-39, -79.88) * mm});
            skLineSegment(sketch, "E223", {"start": v(-39, -79.88) * mm, "end": v(-45, -79.88) * mm});
            skLineSegment(sketch, "E224", {"start": v(-45, -79.88) * mm, "end": v(-45, -106) * mm});
            skLineSegment(sketch, "E225", {"start": v(-45, -106) * mm, "end": v(6, -106) * mm});
            skLineSegment(sketch, "E226", {"start": v(6, -106) * mm, "end": v(6, -79.88) * mm});
            skLineSegment(sketch, "E227", {"start": v(6, -79.88) * mm, "end": v(0, -79.88) * mm});
            skLineSegment(sketch, "E228", {"start": v(0, -79.88) * mm, "end": v(0, -64.88) * mm});
            skLineSegment(sketch, "E229", {"start": v(0, -64.88) * mm, "end": v(6, -64.88) * mm});
            skLineSegment(sketch, "E230", {"start": v(6, -64.88) * mm, "end": v(6, -54.88) * mm});
            skLineSegment(sketch, "E231.trimOffspring", {"start": v(-45, -54.88) * mm, "end": v(-60, -54.88) * mm});
            skCircle(sketch, "E232", {"center": v(15.5, -60.88) * mm, "radius": 1.5 * mm});
            skCircle(sketch, "E233", {"center": v(15.5, -82.88) * mm, "radius": 1 * mm});
            skLineSegment(sketch, "E234", {"start": v(15.5, -60.88) * mm, "end": v(15.5, -82.88) * mm, "construction": true});
            skCircle(sketch, "E235", {"center": v(-54.5, -82.88) * mm, "radius": 1 * mm});
            skLineSegment(sketch, "E236", {"start": v(-19.5, -87.94) * mm, "end": v(-19.5, -82.88) * mm, "construction": true});
            skCircle(sketch, "E237", {"center": v(-54.5, -60.88) * mm, "radius": 1.5 * mm});
            skLineSegment(sketch, "E238", {"start": v(-54.5, -60.88) * mm, "end": v(15.5, -60.88) * mm, "construction": true});
            skLineSegment(sketch, "E239", {"start": v(-19.5, -82.88) * mm, "end": v(-19.5, -60.88) * mm, "construction": true});
            skLineSegment(sketch, "E240", {"start": v(-19.5, -100) * mm, "end": v(-19.5, -116) * mm, "construction": true});
            skLineSegment(sketch, "E241", {"start": v(-55, -116) * mm, "end": v(16, -116) * mm, "construction": true});
            skCircle(sketch, "E242", {"center": v(-55, -116) * mm, "radius": 1.5 * mm});
            skCircle(sketch, "E243", {"center": v(16, -116) * mm, "radius": 1.5 * mm});
            skLineSegment(sketch, "E244", {"start": v(15.5, -82.88) * mm, "end": v(-54.5, -82.88) * mm, "construction": true});
            skSolve(sketch);
        }
        {
            var Q0;
            Q0 = qSketchRegion(id + "F30", true);
            extrude(context, id + "F31", {"entities" : qUnion([Q0]), "depth" : 6 * mm});
        }
        {
            var Q0;
            Q0=makeQuery(id+"F29.opExtrude","SWEPT_FACE",FACE,{"disambiguationData":[OSD([sQuery(id+"F28.wireOp",EDGE,"E217.left")])]});
            var sketch = newSketch(context, id + "F32", { "sketchPlane" : qUnion([Q0])});
            skLineSegment(sketch, "E245", {"start": v(45, 13) * mm, "end": v(45, 13) * mm});
            skLineSegment(sketch, "E246", {"start": v(49, 13) * mm, "end": v(50.5, 26) * mm});
            skLineSegment(sketch, "E247", {"start": v(60, 26) * mm, "end": v(60, 32) * mm});
            skLineSegment(sketch, "E248", {"start": v(60, 32) * mm, "end": v(45, 32) * mm});
            skLineSegment(sketch, "E249", {"start": v(45, 32) * mm, "end": v(45, 28) * mm});
            skLineSegment(sketch, "E250", {"start": v(45, 28) * mm, "end": v(39, 28) * mm});
            skLineSegment(sketch, "E251", {"start": v(39, 28) * mm, "end": v(39, 18) * mm});
            skLineSegment(sketch, "E252", {"start": v(39, 18) * mm, "end": v(45, 18) * mm});
            skLineSegment(sketch, "E253.trimOffspring", {"start": v(45, 18) * mm, "end": v(45, 13) * mm});
            skLineSegment(sketch, "E254", {"start": v(54.5, 26) * mm, "end": v(54.5, 32) * mm, "construction": true});
            skLineSegment(sketch, "E255", {"start": v(45, 13) * mm, "end": v(49, 13) * mm});
            skLineSegment(sketch, "E256", {"start": v(50.5, 26) * mm, "end": v(54.4, 26) * mm});
            skLineSegment(sketch, "E257", {"start": v(54.6, 26) * mm, "end": v(60, 26) * mm});
            skLineSegment(sketch, "E258", {"start": v(54.6, 26) * mm, "end": v(54.5, 26.2) * mm});
            skLineSegment(sketch, "E259", {"start": v(54.5, 26.2) * mm, "end": v(54.4, 26) * mm});
            skSolve(sketch);
        }
        {
            var Q0;
            Q0 = qSketchRegion(id + "F32", true);
            extrude(context, id + "F33", {"entities" : qUnion([Q0]), "depth" : 6 * mm});
        }
    });
